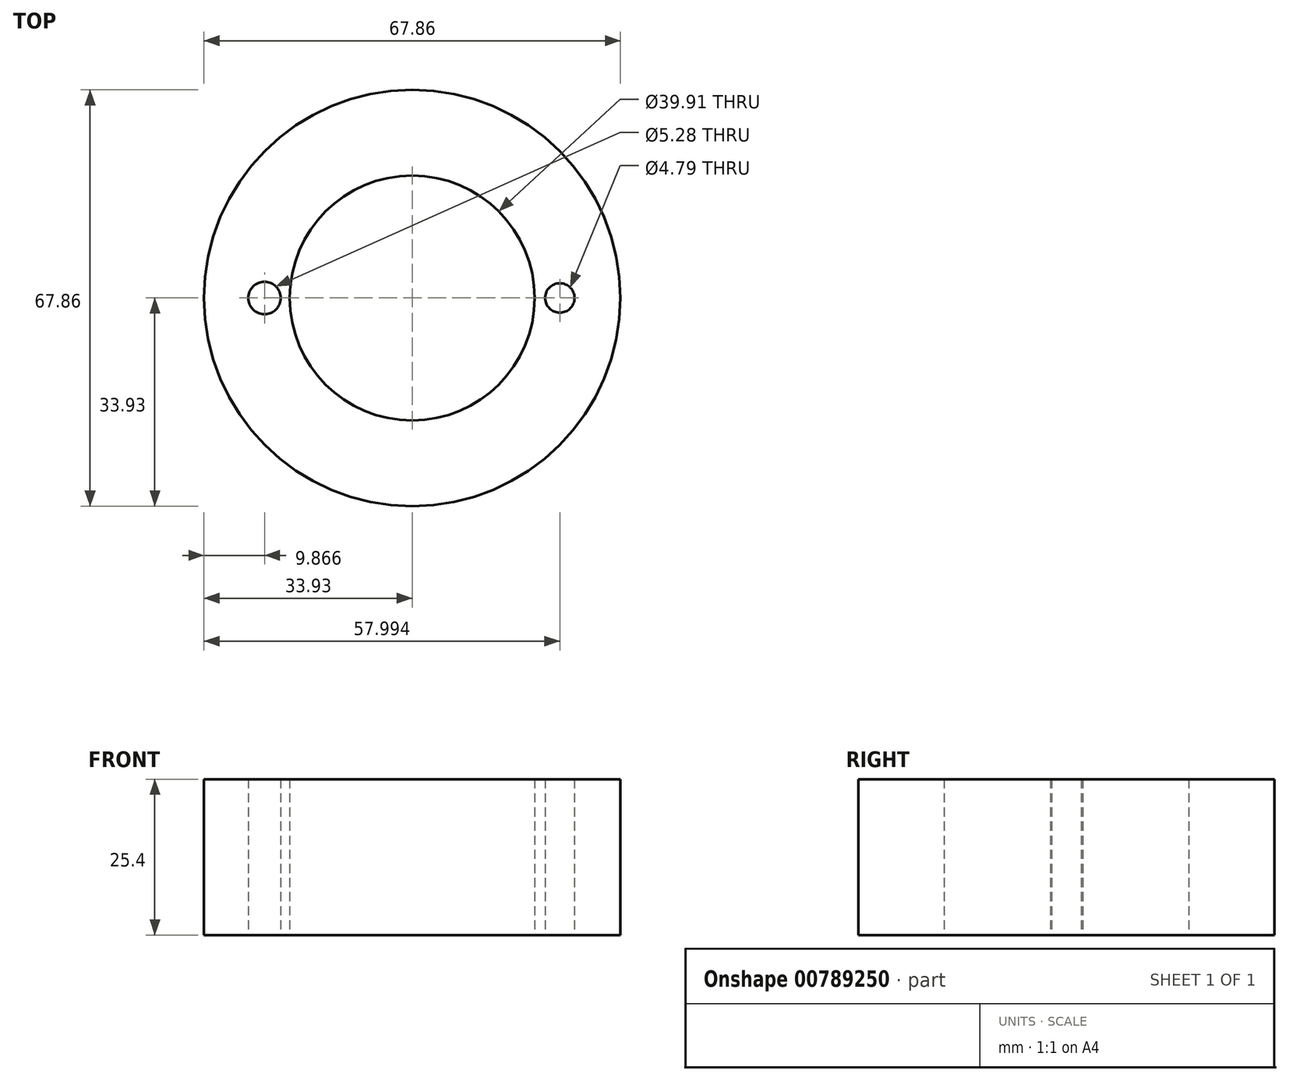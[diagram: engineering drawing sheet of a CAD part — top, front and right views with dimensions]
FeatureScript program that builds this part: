
annotation { "Feature Type Name" : "Feature", "Feature Type Description" : "" }
export const myFeature = defineFeature(function(context is Context, id is Id, definition is map)
    precondition{}
    {
        {
            var Q0;
            Q0=qCreatedBy(makeId("Top.planeOp"),FACE);
            var sketch = newSketch(context, id + "F0", { "sketchPlane" : qUnion([Q0])});
            skCircle(sketch, "E0", {"center": v(24.06, 0) * mm, "radius": 2.4 * mm});
            skCircle(sketch, "E1", {"center": v(-24.06, 0) * mm, "radius": 2.64 * mm});
            skCircle(sketch, "E2", {"center": v(0, 0) * mm, "radius": 33.93 * mm});
            skCircle(sketch, "E3", {"center": v(0, 0) * mm, "radius": 19.95 * mm});
            skSolve(sketch);
        }
        {
            var Q0;
            Q0 = qSketchRegion(id + "F0", true);
            extrude(context, id + "F1", {"entities" : qUnion([Q0]), "depth" : 25.4 * mm, "offsetDistance" : 25.4 * mm});
        }
    });
